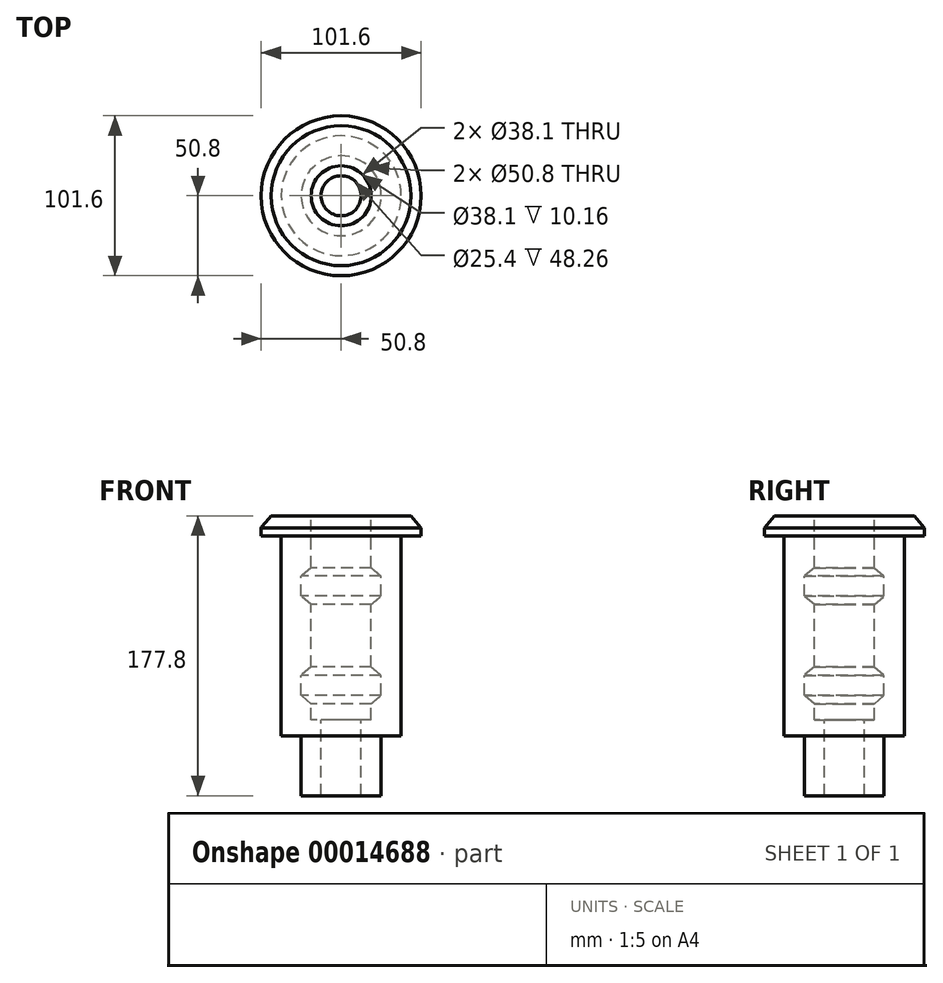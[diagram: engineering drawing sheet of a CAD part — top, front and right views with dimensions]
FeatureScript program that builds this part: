
annotation { "Feature Type Name" : "Feature", "Feature Type Description" : "" }
export const myFeature = defineFeature(function(context is Context, id is Id, definition is map)
    precondition{}
    {
        {
            var Q0;
            Q0=qCreatedBy(makeId("Front.planeOp"),FACE);
            var sketch = newSketch(context, id + "F0", { "sketchPlane" : qUnion([Q0])});
            skLineSegment(sketch, "E0", {"start": v(0, 103.37) * mm, "end": v(0, -114.86) * mm, "construction": true});
            skLineSegment(sketch, "E1", {"start": v(38.1, 63.5) * mm, "end": v(38.1, -63.5) * mm});
            skLineSegment(sketch, "E2", {"start": v(19.05, 106.24) * mm, "end": v(19.05, -152.57) * mm, "construction": true});
            skLineSegment(sketch, "E3", {"start": v(38.1, 63.5) * mm, "end": v(19.05, 63.5) * mm});
            skLineSegment(sketch, "E4", {"start": v(38.1, -63.5) * mm, "end": v(0, -63.5) * mm});
            skLineSegment(sketch, "E5", {"start": v(19.05, 63.5) * mm, "end": v(19.05, 43.18) * mm});
            skLineSegment(sketch, "E6", {"start": v(25.4, 132.18) * mm, "end": v(25.4, -143.64) * mm, "construction": true});
            skPoint(sketch, "E7", {"position": v(38.1, 0) * mm});
            skLineSegment(sketch, "E8", {"start": v(0, 0) * mm, "end": v(186.2, 0) * mm, "construction": true});
            skLineSegment(sketch, "E9", {"start": v(19.05, 43.18) * mm, "end": v(25.4, 37.85) * mm});
            skLineSegment(sketch, "E10", {"start": v(25.4, 37.85) * mm, "end": v(25.4, 25.15) * mm});
            skLineSegment(sketch, "E11", {"start": v(25.4, 25.15) * mm, "end": v(19.05, 19.82) * mm});
            skLineSegment(sketch, "E12", {"start": v(19.05, 19.82) * mm, "end": v(19.05, 0) * mm});
            skLineSegment(sketch, "E13.MirrorCS", {"start": v(19.05, -19.82) * mm, "end": v(19.05, 0) * mm});
            skLineSegment(sketch, "E14.MirrorCS", {"start": v(25.4, -25.15) * mm, "end": v(19.05, -19.82) * mm});
            skLineSegment(sketch, "E15.MirrorCS", {"start": v(25.4, -37.85) * mm, "end": v(25.4, -25.15) * mm});
            skLineSegment(sketch, "E16.MirrorCS", {"start": v(19.05, -43.18) * mm, "end": v(25.4, -37.85) * mm});
            skLineSegment(sketch, "E17.MirrorCS", {"start": v(19.05, -53.34) * mm, "end": v(19.05, -43.18) * mm});
            skLineSegment(sketch, "E18", {"start": v(19.05, -53.34) * mm, "end": v(12.7, -53.34) * mm});
            skPoint(sketch, "E18.endSnap0", {"position": v(19.05, -53.34) * mm});
            skLineSegment(sketch, "E19", {"start": v(12.7, -53.34) * mm, "end": v(12.7, -63.5) * mm});
            skPoint(sketch, "E20.orphan", {"position": v(19.05, -63.5) * mm});
            skLineSegment(sketch, "E21", {"start": v(38.1, 63.5) * mm, "end": v(55.1, 63.5) * mm});
            skLineSegment(sketch, "E22", {"start": v(55.1, 63.5) * mm, "end": v(44.45, 76.2) * mm});
            skLineSegment(sketch, "E23", {"start": v(44.45, 76.2) * mm, "end": v(19.05, 76.2) * mm});
            skLineSegment(sketch, "E24", {"start": v(19.05, 76.2) * mm, "end": v(19.05, 63.5) * mm});
            skLineSegment(sketch, "E25", {"start": v(12.7, -63.5) * mm, "end": v(12.7, -101.6) * mm});
            skLineSegment(sketch, "E26", {"start": v(12.7, -101.6) * mm, "end": v(25.4, -101.6) * mm});
            skLineSegment(sketch, "E27", {"start": v(25.4, -101.6) * mm, "end": v(25.4, -63.5) * mm});
            skPoint(sketch, "E28", {"position": v(25.4, 31.5) * mm});
            skPoint(sketch, "E29", {"position": v(25.4, -31.5) * mm});
            skSolve(sketch);
        }
        {
            var Q0;
            Q0=makeQuery(id+"F0.imprint","IMPRINT",FACE,{"disambiguationData":[TD([[makeQuery(id+"F0.imprint","IMPRINT",EDGE,{"derivedFrom":sQuery(id+"F0.wireOp",EDGE,"E3")}),-1.0]])]});
            var Q1;
            {var subQ3=sQuery(id+"F0.wireOp",EDGE,"E1");Q1=makeQuery(id+"F0.imprint","IMPRINT",FACE,{"disambiguationData":[TD([[makeQuery(id+"F0.imprint","IMPRINT",EDGE,{"derivedFrom":subQ3}),-1.0]])]});}
            var Q2;
            {var subQ1=sQuery(id+"F0.wireOp",EDGE,"E25");Q2=makeQuery(id+"F0.imprint","IMPRINT",FACE,{"disambiguationData":[TD([[makeQuery(id+"F0.imprint","IMPRINT",EDGE,{"derivedFrom":subQ1}),1.0]])]});}
            var Q3;
            Q3=sQuery(id+"F0.wireOp",EDGE,"E0");
            revolve(context, id + "F1", {"entities" : qUnion([Q0, Q1, Q2]), "axis" : qUnion([Q3]), "revolveType" : RevolveType.FULL});
        }
        {
            var Q0;
            Q0=makeQuery(id+"F1.opRevolve","SWEPT_FACE",FACE,{"disambiguationData":[OSD([sQuery(id+"F0.wireOp",EDGE,"E21")])]});
            var sketch = newSketch(context, id + "F2", { "sketchPlane" : qUnion([Q0])});
            skCircle(sketch, "E30", {"center": v(0, 0) * mm, "radius": 50.8 * mm});
            skCircle(sketch, "E31", {"center": v(0, 0) * mm, "radius": 63.5 * mm});
            skSolve(sketch);
        }
        {
            var Q0;
            Q0=makeQuery(id+"F2.imprint","IMPRINT",FACE,{"disambiguationData":[TD([[makeQuery(id+"F2.imprint","IMPRINT",EDGE,{"derivedFrom":sQuery(id+"F2.wireOp",EDGE,"E30")}),-1.0]])]});
            extrude(context, id + "F3", {"entities" : qUnion([Q0]), "operationType" : NewBodyOperationType.REMOVE, "endBound" : BoundingType.THROUGH_ALL, "oppositeDirection" : true, "depth" : 25.4 * mm});
        }
    });
